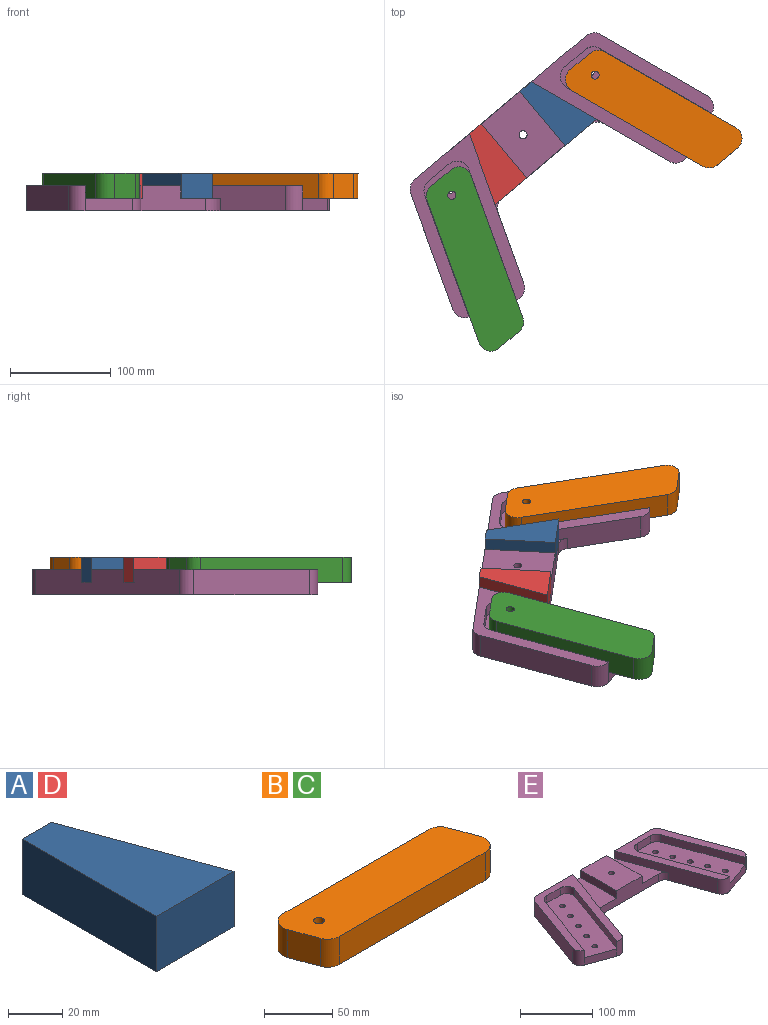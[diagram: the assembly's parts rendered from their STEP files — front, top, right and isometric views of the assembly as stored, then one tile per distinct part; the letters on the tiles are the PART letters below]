
ASSEMBLY  parts=5 mates=11
PART A: 6 faces, bbox 40.7x70x25 mm
  f0: plane 25x15.2mm, normal (0,1,0), area 380mm2, adj f1,f3,f4,f5
  f1: plane 70x25mm, normal (-1,0,0), area 1750mm2, adj f0,f2,f4,f5
  f2: plane 40.68x25mm, normal (0,-1,0), area 1016.9mm2, adj f1,f3,f4,f5
  f3: plane 70x25.48mm, normal (0.94,0.34,0), area 1862.3mm2, adj f0,f2,f4,f5
  f4: plane 70x40.68mm, normal (0,0,1), area 1955.7mm2, adj f0,f1,f2,f3
  f5: plane 70x40.68mm, normal (0,0,-1), area 1955.7mm2, adj f0,f1,f2,f3
PART B: 11 faces, bbox 184.3x49.5x25 mm
  f0: plane 25x24.5mm, normal (-0.94,-0.34,0), area 651.8mm2, adj f1,f7,f8,f9
  f1: cylinder r=12.5mm len=25mm, axis (0,0,-1), area 381.8mm2, adj f0,f2,f8,f9
  f2: plane 150.4x25mm, normal (0,-1,0), area 3759.9mm2, adj f1,f3,f8,f9
  f3: cylinder r=12.5mm len=25mm, axis (0,0,-1), area 600mm2, adj f2,f4,f8,f9
  f4: plane 25x24.5mm, normal (0.94,0.34,0), area 651.8mm2, adj f3,f5,f8,f9
  f5: cylinder r=12.5mm len=25mm, axis (0,0,-1), area 381.8mm2, adj f4,f6,f8,f9
  f6: plane 150.4x25mm, normal (0,1,0), area 3759.9mm2, adj f5,f7,f8,f9
  f7: cylinder r=12.5mm len=25mm, axis (0,0,-1), area 600mm2, adj f0,f6,f8,f9
  f8: plane 184.31x49.5mm, normal (0,0,1), area 8537mm2, adj f0,f1,f2,f3,f4,f5,f6,f7
  f9: plane 184.31x49.5mm, normal (0,0,-1), area 8537mm2, adj f0,f1,f2,f3,f4,f5,f6,f7
  f10: cylinder r=4mm len=25mm, axis (0,0,1), area 628.3mm2, adj f8,f9
PART C: same geometry as B
PART D: same geometry as A
PART E: 47 faces, bbox 331.1x156.9x25 mm
  f0: plane 70x50mm, normal (0,0,1), area 3449.7mm2, adj f2,f8,f40,f43,f46
  f1: plane 156.93x125.35mm, normal (0,0,1), area 4465.6mm2, adj f6,f7,f8,f14,f15,f16,f18,f19
  f2: plane 113.82x25mm, normal (0,-1,0), area 2047.8mm2, adj f0,f17,f40,f41,f42,f43,f44,f45
  f3: plane 46.98x17.1mm, normal (-0.34,-0.94,0), area 625mm2, adj f11,f12,f17,f29
  f4: plane 156.93x125.35mm, normal (0,0,1), area 4465.6mm2, adj f8,f9,f10,f11,f12,f13,f24,f25
  f5: plane 46.98x17.1mm, normal (0.34,-0.94,0), area 625mm2, adj f15,f16,f17,f23
  f6: plane 114.83x41.79mm, normal (0.94,0.34,0), area 3054.9mm2, adj f1,f7,f16,f17
  f7: cylinder r=12.5mm len=25mm, axis (0,0,-1), area 381.8mm2, adj f1,f6,f8,f17
  f8: plane 222.5x25mm, normal (0,1,0), area 5182.7mm2, adj f0,f1,f4,f7,f9,f13,f14,f17
  f9: cylinder r=12.5mm len=25mm, axis (0,0,-1), area 381.8mm2, adj f4,f8,f10,f17
  f10: plane 114.83x41.79mm, normal (-0.94,0.34,0), area 3054.9mm2, adj f4,f9,f11,f17
  f11: cylinder r=12.5mm len=25mm, axis (0,0,-1), area 490.9mm2, adj f3,f4,f10,f17,f28
  f12: cylinder r=12.5mm len=25mm, axis (0,0,-1), area 490.9mm2, adj f3,f4,f13,f17,f24
  f13: plane 148.7x54.12mm, normal (0.94,-0.34,0), area 2915.6mm2, adj f4,f8,f12,f17,f44,f45
  f14: plane 148.7x54.12mm, normal (-0.94,-0.34,0), area 2915.6mm2, adj f1,f8,f15,f17,f41,f42
  f15: cylinder r=12.5mm len=25mm, axis (0,0,-1), area 490.9mm2, adj f1,f5,f14,f17,f18
  f16: cylinder r=12.5mm len=25mm, axis (0,0,-1), area 490.9mm2, adj f1,f5,f6,f17,f19
  f17: plane 331.08x156.93mm, normal (0,0,-1), area 30287mm2, adj f2,f3,f5,f6,f7,f8,f9,f10
  f18: plane 129.4x47.1mm, normal (0.94,0.34,0), area 1721.3mm2, adj f1,f15,f22,f23
  f19: plane 120.85x43.98mm, normal (-0.94,-0.34,0), area 1607.5mm2, adj f1,f16,f20,f23
  f20: cylinder r=12.5mm len=12.5mm, axis (0,0,1), area 190.9mm2, adj f1,f19,f21,f23
  f21: plane 26.6x12.5mm, normal (0,-1,0), area 332.6mm2, adj f1,f20,f22,f23
  f22: cylinder r=12.5mm len=16.78mm, axis (0,0,1), area 300mm2, adj f1,f18,f21,f23
  f23: plane 146.17x94.84mm, normal (0,0,1), area 6984.3mm2, adj f5,f18,f19,f20,f21,f22,f35,f36
  f24: plane 129.4x47.1mm, normal (-0.94,0.34,0), area 1721.3mm2, adj f4,f12,f25,f29
  f25: cylinder r=12.5mm len=16.78mm, axis (0,0,1), area 300mm2, adj f4,f24,f26,f29
  f26: plane 26.6x12.5mm, normal (0,-1,0), area 332.6mm2, adj f4,f25,f27,f29
  f27: cylinder r=12.5mm len=12.5mm, axis (0,0,1), area 190.9mm2, adj f4,f26,f28,f29
  f28: plane 120.85x43.98mm, normal (0.94,-0.34,0), area 1607.5mm2, adj f4,f11,f27,f29
  f29: plane 146.17x94.84mm, normal (0,0,1), area 6984.3mm2, adj f3,f24,f25,f26,f27,f28,f30,f31
  f30: cylinder r=4mm len=12.5mm, axis (0,0,-1), area 314.2mm2, adj f17,f29
  f31: cylinder r=4mm len=12.5mm, axis (0,0,-1), area 314.2mm2, adj f17,f29
  f32: cylinder r=4mm len=12.5mm, axis (0,0,-1), area 314.2mm2, adj f17,f29
  f33: cylinder r=4mm len=12.5mm, axis (0,0,-1), area 314.2mm2, adj f17,f29
  f34: cylinder r=4mm len=12.5mm, axis (0,0,-1), area 314.2mm2, adj f17,f29
  f35: cylinder r=4mm len=12.5mm, axis (0,0,-1), area 314.2mm2, adj f17,f23
  f36: cylinder r=4mm len=12.5mm, axis (0,0,-1), area 314.2mm2, adj f17,f23
  f37: cylinder r=4mm len=12.5mm, axis (0,0,-1), area 314.2mm2, adj f17,f23
  f38: cylinder r=4mm len=12.5mm, axis (0,0,-1), area 314.2mm2, adj f17,f23
  f39: cylinder r=4mm len=12.5mm, axis (0,0,-1), area 314.2mm2, adj f17,f23
  f40: plane 70x12.5mm, normal (1,0,0), area 875mm2, adj f0,f2,f8,f41
  f41: plane 78.22x43.66mm, normal (0,0,1), area 1968.8mm2, adj f2,f8,f14,f40,f42
  f42: cylinder r=12.5mm len=12.5mm, axis (0,0,1), area 190.9mm2, adj f2,f14,f17,f41
  f43: plane 70x12.5mm, normal (-1,0,0), area 875mm2, adj f0,f2,f8,f44
  f44: plane 78.22x43.66mm, normal (0,0,1), area 1968.8mm2, adj f2,f8,f13,f43,f45
  f45: cylinder r=12.5mm len=12.5mm, axis (0,0,1), area 190.9mm2, adj f2,f13,f17,f44
  f46: cylinder r=4mm len=25mm, axis (0,0,1), area 628.3mm2, adj f0,f17
PLACE A rot(axis=(0,0,1),40deg) t=(-95.03,19.3,-87.26)mm
PLACE B rot(axis=(0.97,-0.26,0),180deg) t=(22.84,20.07,-62.26)mm
PLACE C rot(axis=(0,0,-1),70deg) t=(-154.56,-128.79,-87.26)mm
PLACE D rot(axis=(0.34,-0.94,0),180deg) t=(-133.33,-12.84,-62.26)mm
PLACE E rot(axis=(0,0,1),40deg) t=(-106.88,-5.48,-99.76)mm fixed
MATE planar A.f3 <-> E.f14  axis (0.5,0.87,0) through (-66.3,28.52,-74.76)mm
MATE planar C.f9 <-> E.f31  axis (0,0,-1) through (-132.83,-116.13,-87.26)mm
MATE planar A.f1 <-> E.f40  axis (-0.77,-0.64,0) through (-110.2,37.37,-62.26)mm
MATE planar D.f1 <-> E.f43  axis (0.77,0.64,0) through (-126,-21.58,-74.76)mm
MATE planar B.f0 <-> C.f0  axis (-0.64,0.77,0) through (-50.32,67.24,-62.26)mm
MATE planar A.f5 <-> E.f41  axis (0,0,-1) through (-72.84,16.09,-87.26)mm
MATE planar E.f13 <-> D.f3  axis (0.94,0.34,0) through (-128.52,-91.43,-85.03)mm
MATE planar D.f4 <-> E.f44  axis (0,0,-1) through (-134.03,-35.26,-87.26)mm
MATE planar E.f24 <-> C.f6  axis (-0.94,-0.34,0) through (-137.05,-104.53,-81.01)mm
MATE planar B.f6 <-> E.f18  axis (-0.5,-0.87,0) through (-58.52,38.46,-74.76)mm
MATE planar E.f23 <-> B.f8  axis (0,0,1) through (5.11,30.17,-87.26)mm
